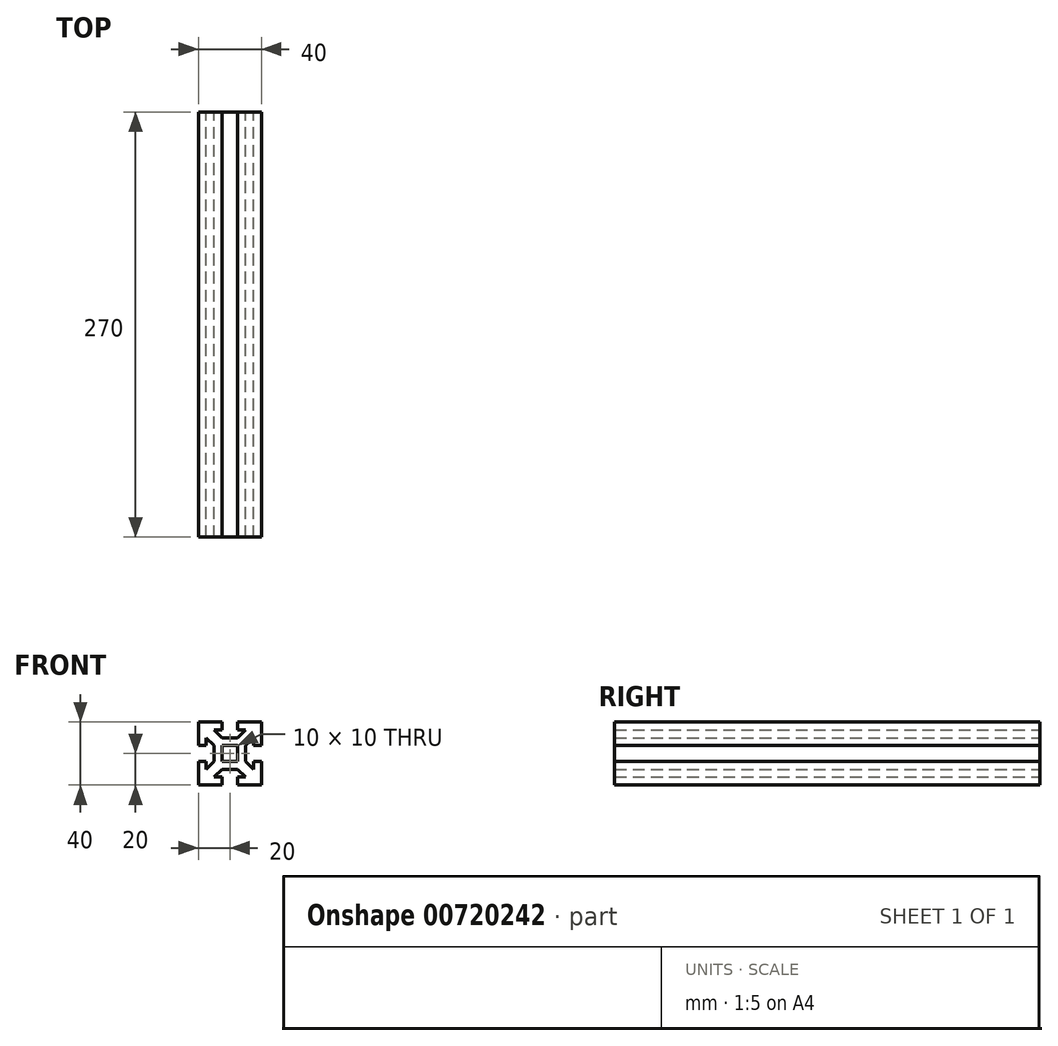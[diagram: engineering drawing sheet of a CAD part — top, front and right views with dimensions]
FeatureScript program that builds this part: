
annotation { "Feature Type Name" : "Feature", "Feature Type Description" : "" }
export const myFeature = defineFeature(function(context is Context, id is Id, definition is map)
    precondition{}
    {
        {
            var Q0;
            Q0=qCreatedBy(makeId("Front.planeOp"),FACE);
            var sketch = newSketch(context, id + "F0", { "sketchPlane" : qUnion([Q0])});
            skLineSegment(sketch, "E0.bottom", {"start": v(20, 20) * mm, "end": v(5, 20) * mm});
            skLineSegment(sketch, "E0.top", {"start": v(20, -20) * mm, "end": v(5, -20) * mm});
            skLineSegment(sketch, "E0.left", {"start": v(20, 20) * mm, "end": v(20, 5) * mm});
            skLineSegment(sketch, "E0.right", {"start": v(-20, 20) * mm, "end": v(-20, 5) * mm});
            skPoint(sketch, "E0.middle", {"position": v(0, 0) * mm});
            skLineSegment(sketch, "E1", {"start": v(0, 20) * mm, "end": v(0, -20) * mm, "construction": true});
            skLineSegment(sketch, "E2", {"start": v(-20, 0) * mm, "end": v(20, 0) * mm, "construction": true});
            skLineSegment(sketch, "E3", {"start": v(-20, 5) * mm, "end": v(-15, 5) * mm});
            skLineSegment(sketch, "E4", {"start": v(-20, -5) * mm, "end": v(-15, -5) * mm});
            skLineSegment(sketch, "E5", {"start": v(-5, 20) * mm, "end": v(-5, 15) * mm});
            skLineSegment(sketch, "E6", {"start": v(5, 20) * mm, "end": v(5, 15) * mm});
            skLineSegment(sketch, "E7", {"start": v(-10, 15) * mm, "end": v(-5, 15) * mm});
            skLineSegment(sketch, "E8", {"start": v(-10, -15) * mm, "end": v(-5, -15) * mm});
            skLineSegment(sketch, "E9", {"start": v(15, 10) * mm, "end": v(15, 5) * mm});
            skLineSegment(sketch, "E10", {"start": v(-15, 10) * mm, "end": v(-10, 5) * mm});
            skLineSegment(sketch, "E11", {"start": v(-10, 15) * mm, "end": v(-5, 10) * mm});
            skLineSegment(sketch, "E12", {"start": v(-15, -10) * mm, "end": v(-10, -5) * mm});
            skLineSegment(sketch, "E13", {"start": v(-10, -15) * mm, "end": v(-5, -10) * mm});
            skLineSegment(sketch, "E14.trimOffspring", {"start": v(20, -5) * mm, "end": v(20, -20) * mm});
            skLineSegment(sketch, "E15.trimOffspring", {"start": v(-20, -5) * mm, "end": v(-20, -20) * mm});
            skLineSegment(sketch, "E16.trimOffspring", {"start": v(-5, -20) * mm, "end": v(-20, -20) * mm});
            skLineSegment(sketch, "E17.trimOffspring", {"start": v(-5, 20) * mm, "end": v(-20, 20) * mm});
            skLineSegment(sketch, "E18.trimOffspring", {"start": v(5, 15) * mm, "end": v(10, 15) * mm});
            skLineSegment(sketch, "E19.trimOffspring", {"start": v(-15, -5) * mm, "end": v(-15, -10) * mm});
            skLineSegment(sketch, "E20.trimOffspring", {"start": v(15, -5) * mm, "end": v(15, -10) * mm});
            skLineSegment(sketch, "E21.trimOffspring", {"start": v(5, -15) * mm, "end": v(10, -15) * mm});
            skLineSegment(sketch, "E22.trimOffspring", {"start": v(-5, 5) * mm, "end": v(-5, -5) * mm});
            skLineSegment(sketch, "E23.trimOffspring", {"start": v(5, 5) * mm, "end": v(5, -5) * mm});
            skLineSegment(sketch, "E24.trimOffspring", {"start": v(15, 5) * mm, "end": v(20, 5) * mm});
            skLineSegment(sketch, "E25.trimOffspring", {"start": v(15, -5) * mm, "end": v(20, -5) * mm});
            skLineSegment(sketch, "E26.trimOffspring", {"start": v(5, -15) * mm, "end": v(5, -20) * mm});
            skLineSegment(sketch, "E27.trimOffspring", {"start": v(-5, -15) * mm, "end": v(-5, -20) * mm});
            skLineSegment(sketch, "E28.trimOffspring", {"start": v(-5, -5) * mm, "end": v(5, -5) * mm});
            skLineSegment(sketch, "E29.trimOffspring", {"start": v(-5, 5) * mm, "end": v(5, 5) * mm});
            skLineSegment(sketch, "E30", {"start": v(10, 5) * mm, "end": v(10, -5) * mm});
            skLineSegment(sketch, "E31", {"start": v(-5, 10) * mm, "end": v(5, 10) * mm});
            skLineSegment(sketch, "E32", {"start": v(-10, 5) * mm, "end": v(-10, -5) * mm});
            skLineSegment(sketch, "E33", {"start": v(-5, -10) * mm, "end": v(5, -10) * mm});
            skLineSegment(sketch, "E34.trimOffspring", {"start": v(-15, 10) * mm, "end": v(-15, 5) * mm});
            skPoint(sketch, "E35.orphan", {"position": v(20, 15) * mm});
            skPoint(sketch, "E36.orphan", {"position": v(20, -15) * mm});
            skPoint(sketch, "E37.orphan", {"position": v(15, -20) * mm});
            skPoint(sketch, "E38.orphan", {"position": v(-15, -20) * mm});
            skLineSegment(sketch, "E39.trimOffspring", {"start": v(-5, 0) * mm, "end": v(0, -5) * mm});
            skLineSegment(sketch, "E40.trimOffspring", {"start": v(-5, 0) * mm, "end": v(0, 5) * mm});
            skLineSegment(sketch, "E41.trimOffspring", {"start": v(0, 5) * mm, "end": v(5, 0) * mm});
            skLineSegment(sketch, "E42.trimOffspring", {"start": v(5, 10) * mm, "end": v(10, 15) * mm});
            skLineSegment(sketch, "E43.trimOffspring", {"start": v(10, 5) * mm, "end": v(15, 10) * mm});
            skLineSegment(sketch, "E44.trimOffspring", {"start": v(10, -5) * mm, "end": v(15, -10) * mm});
            skLineSegment(sketch, "E45.trimOffspring", {"start": v(5, -10) * mm, "end": v(10, -15) * mm});
            skLineSegment(sketch, "E46.trimOffspring", {"start": v(0, -5) * mm, "end": v(5, 0) * mm});
            skSolve(sketch);
        }
        {
            var Q0;
            Q0=makeQuery(id+"F0.imprint","IMPRINT",FACE,{"disambiguationData":[TD([[makeQuery(id+"F0.imprint","IMPRINT",EDGE,{"derivedFrom":sQuery(id+"F0.wireOp",EDGE,"E0.bottom")}),1.0]])]});
            extrude(context, id + "F1", {"entities" : qUnion([Q0]), "depth" : 270 * mm, "offsetDistance" : 25 * mm});
        }
    });
